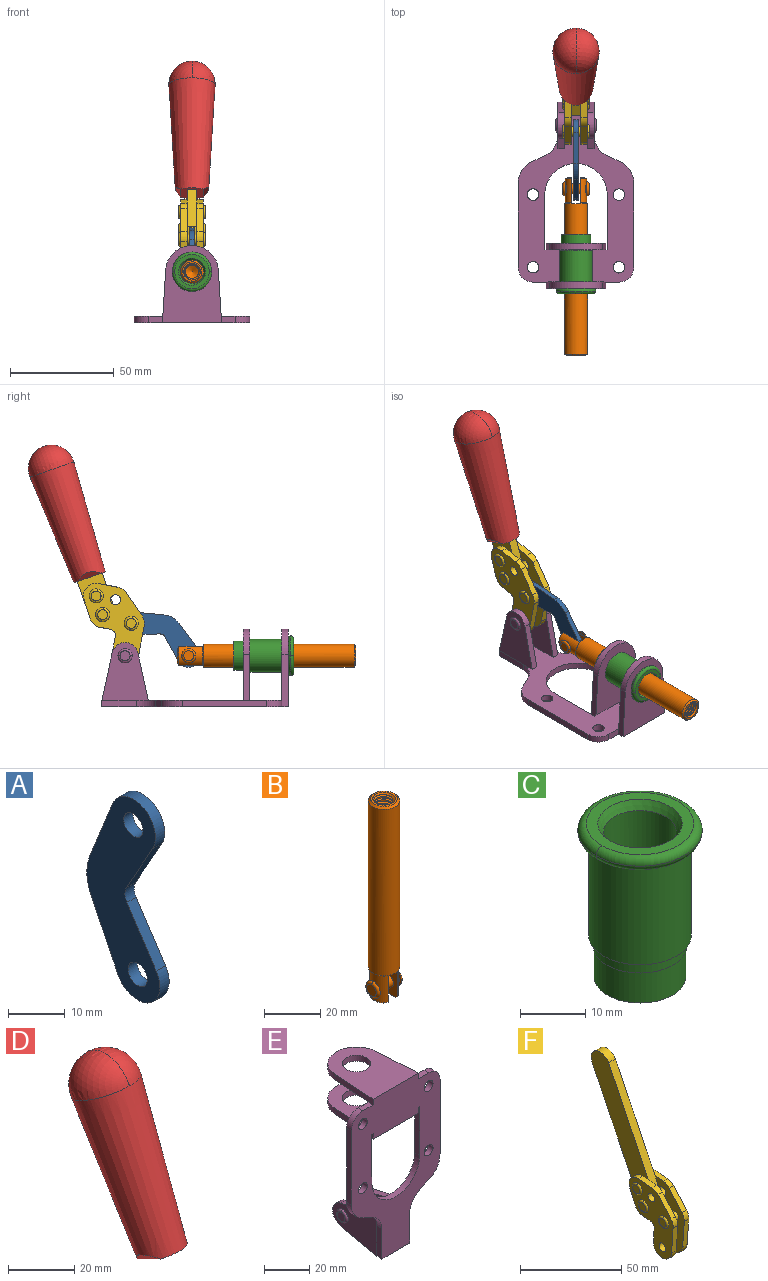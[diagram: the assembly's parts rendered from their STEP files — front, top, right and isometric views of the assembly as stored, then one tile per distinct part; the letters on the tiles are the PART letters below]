
ASSEMBLY  parts=6 mates=6
PART A: 12 faces, bbox 2.3x18.2x42.8 mm
  f0: cylinder r=2.4mm len=4.8mm, axis (1,0,0), area 34.9mm2, adj f4,f11
  f1: cylinder r=10.41mm len=8.47mm, axis (1,0,0), area 20.2mm2, adj f4,f9,f10,f11
  f2: cylinder r=3.05mm len=3.16mm, axis (1,0,0), area 7.7mm2, adj f4,f6,f7,f11
  f3: cylinder r=2.4mm len=4.8mm, axis (1,0,0), area 34.9mm2, adj f4,f11
  f4: plane 42.81x18.23mm, normal (-1,0,0), area 414.1mm2, adj f0,f1,f2,f3,f5,f6,f7,f8
  f5: cylinder r=5.54mm len=10.67mm, axis (1,0,0), area 41.8mm2, adj f4,f6,f10,f11
  f6: plane 11.66x6.53mm, normal (0,-0.87,-0.49), area 30.9mm2, adj f2,f4,f5,f11
  f7: plane 11.17x7.33mm, normal (0,-0.84,0.55), area 30.9mm2, adj f2,f4,f8,f11
  f8: cylinder r=5.54mm len=10.51mm, axis (1,0,0), area 41.8mm2, adj f4,f7,f9,f11
  f9: plane 13.67x6.67mm, normal (0,0.9,-0.44), area 35.1mm2, adj f1,f4,f8,f11
  f10: plane 14.1x5.7mm, normal (0,0.93,0.37), area 35.1mm2, adj f1,f4,f5,f11
  f11: plane 42.81x18.23mm, normal (1,0,0), area 414.1mm2, adj f0,f1,f2,f3,f5,f6,f7,f8
PART B: 48 faces, bbox 12.6x11.1x86.1 mm
  f0: torus R=2.41mm, axis (-1,0,0), area 15mm2, adj f30,f32,f34
  f1: torus R=2.41mm, axis (-1,0,0), area 15mm2, adj f29,f31,f33
  f2: cylinder r=5.54mm len=72.39mm, axis (0,0,1), area 2518.5mm2, adj f3,f4,f42,f43
  f3: cone r=5.54mm half-angle=45deg, axis (0,0,1), area 7.6mm2, adj f2,f5,f41
  f4: cone r=5.54mm half-angle=45deg, axis (0,0,-1), area 34.9mm2, adj f2,f39
  f5: cylinder r=5.08mm len=11.48mm, axis (0,0,1), area 108.3mm2, adj f3,f7,f8,f41
  f6: cylinder r=2.41mm len=4.83mm, axis (-1,0,0), area 71.2mm2, adj f40,f41
  f7: cylinder r=2.41mm len=4.83mm, axis (-1,0,0), area 7.6mm2, adj f5,f34
  f8: cone r=5.08mm half-angle=45deg, axis (0,0,1), area 10.6mm2, adj f5,f37,f41
  f9: cone r=3.98mm half-angle=45deg, axis (0,0,1), area 17.6mm2, adj f27,f39,f45,f46,f47
  f10: cylinder r=2.41mm len=4.83mm, axis (-1,0,0), area 7.6mm2, adj f33,f38
  f11: cylinder r=3.2mm len=6.4mm, axis (0,0,1), area 78.4mm2, adj f12,f28,f44,f45,f47
  f12: cylinder r=3.2mm len=6.4mm, axis (0,0,1), area 10.5mm2, adj f11,f13,f45,f47
  f13: cylinder r=3.2mm len=6.4mm, axis (0,0,1), area 10.5mm2, adj f12,f14,f45,f47
  f14: cylinder r=3.2mm len=6.4mm, axis (0,0,1), area 10.5mm2, adj f13,f15,f45,f47
  f15: cylinder r=3.2mm len=6.4mm, axis (0,0,1), area 10.5mm2, adj f14,f16,f45,f47
  f16: cylinder r=3.2mm len=6.4mm, axis (0,0,1), area 10.5mm2, adj f15,f17,f45,f47
  f17: cylinder r=3.2mm len=6.4mm, axis (0,0,1), area 10.5mm2, adj f16,f18,f45,f47
  f18: cylinder r=3.2mm len=6.4mm, axis (0,0,1), area 10.5mm2, adj f17,f19,f45,f47
  f19: cylinder r=3.2mm len=6.4mm, axis (0,0,1), area 10.5mm2, adj f18,f20,f45,f47
  f20: cylinder r=3.2mm len=6.4mm, axis (0,0,1), area 10.5mm2, adj f19,f21,f45,f47
  f21: cylinder r=3.2mm len=6.4mm, axis (0,0,1), area 10.5mm2, adj f20,f22,f45,f47
  f22: cylinder r=3.2mm len=6.4mm, axis (0,0,1), area 10.5mm2, adj f21,f23,f45,f47
  f23: cylinder r=3.2mm len=6.4mm, axis (0,0,1), area 10.5mm2, adj f22,f24,f45,f47
  f24: cylinder r=3.2mm len=6.4mm, axis (0,0,1), area 10.5mm2, adj f23,f25,f45,f47
  f25: cylinder r=3.2mm len=6.4mm, axis (0,0,1), area 10.5mm2, adj f24,f26,f45,f47
  f26: cylinder r=3.2mm len=6.4mm, axis (0,0,1), area 10.5mm2, adj f25,f27,f45,f47
  f27: cylinder r=3.2mm len=6.4mm, axis (0,0,1), area 7.4mm2, adj f9,f26,f45,f47
  f28: cone r=3.2mm half-angle=60deg, axis (0,0,1), area 37.2mm2, adj f11
  f29: plane 4.83x4.83mm, normal (-1,0,0), area 18.3mm2, adj f1,f31
  f30: plane 4.83x4.83mm, normal (1,0,0), area 18.3mm2, adj f0,f32
  f31: torus R=2.41mm, axis (-1,0,0), area 15mm2, adj f1,f29,f33
  f32: torus R=2.41mm, axis (-1,0,0), area 15mm2, adj f0,f30,f34
  f33: plane 6.83x6.83mm, normal (1,0,0), area 18.3mm2, adj f1,f10,f31
  f34: plane 6.83x6.83mm, normal (-1,0,0), area 18.3mm2, adj f0,f7,f32
  f35: cone r=5.08mm half-angle=45deg, axis (0,0,1), area 10.6mm2, adj f36,f38,f40
  f36: plane 7.25x1.97mm, normal (0,0,-1), area 10mm2, adj f35,f40
  f37: plane 7.25x1.97mm, normal (0,0,-1), area 10mm2, adj f8,f41
  f38: cylinder r=5.08mm len=11.48mm, axis (0,0,1), area 108.3mm2, adj f10,f35,f40,f42
  f39: plane 9.55x9.55mm, normal (0,0,1), area 22mm2, adj f4,f9
  f40: plane 12.76x10.09mm, normal (1,0,0), area 95.7mm2, adj f6,f35,f36,f38,f42,f43
  f41: plane 12.76x10.09mm, normal (-1,0,0), area 95.7mm2, adj f3,f5,f6,f8,f37,f43
  f42: cone r=5.54mm half-angle=45deg, axis (0,0,1), area 7.6mm2, adj f2,f38,f40
  f43: plane 11.07x4.7mm, normal (0,0,-1), area 50.4mm2, adj f2,f40,f41
  f44: plane 0.89x0.62mm, normal (-1,0,0), area 0.3mm2, adj f11,f45,f46,f47
  f45: bspline ~24.8x7.63mm, area 266.6mm2, adj f9,f11,f12,f13,f14,f15,f16,f17
  f46: bspline ~24.87x7.63mm, area 73.6mm2, adj f9,f44,f45,f47
  f47: bspline ~24.98x7.63mm, area 272.5mm2, adj f9,f11,f12,f13,f14,f15,f16,f17
PART C: 15 faces, bbox 20.6x20.6x28.7 mm
  f0: torus R=8.26mm, axis (0,0,1), area 56.8mm2, adj f1,f10,f12
  f1: torus R=8.26mm, axis (0,0,1), area 56.8mm2, adj f0,f6,f13
  f2: cylinder r=5.59mm len=25.91mm, axis (0,0,1), area 909.6mm2, adj f3,f4
  f3: cone r=6.86mm half-angle=45deg, axis (0,0,-1), area 70.2mm2, adj f2,f14
  f4: cone r=6.47mm half-angle=30deg, axis (0,0,1), area 66.7mm2, adj f2,f13
  f5: cylinder r=7.04mm len=14.07mm, axis (0,0,1), area 252.6mm2, adj f11,f14
  f6: torus R=8.26mm, axis (0,0,1), area 56.8mm2, adj f1,f12,f13
  f7: cylinder r=7.16mm len=14.33mm, axis (0,0,1), area 91.5mm2, adj f9,f11
  f8: cylinder r=7.86mm len=18.42mm, axis (0,0,1), area 909.6mm2, adj f9,f10
  f9: plane 15.72x15.72mm, normal (0,0,-1), area 33mm2, adj f7,f8
  f10: plane 16.51x16.51mm, normal (0,0,-1), area 19.9mm2, adj f0,f8,f12
  f11: plane 14.33x14.33mm, normal (0,0,-1), area 5.7mm2, adj f5,f7
  f12: torus R=8.26mm, axis (0,0,1), area 56.8mm2, adj f0,f6,f10
  f13: plane 16.51x16.51mm, normal (0,0,1), area 82.7mm2, adj f1,f4,f6
  f14: plane 14.07x14.07mm, normal (0,0,-1), area 7.8mm2, adj f3,f5
PART D: 11 faces, bbox 22.3x42.6x64.5 mm
  f0: sphere r=11.13mm, area 411.4mm2, adj f1,f8
  f1: cone r=11.11mm half-angle=3.3deg, axis (0,0.44,0.9), area 3251.8mm2, adj f0,f7,f8,f9,f10
  f2: cylinder r=6.16mm len=11.7mm, axis (1,0,0), area 89.5mm2, adj f3,f4,f5,f6
  f3: plane 60.23x36.75mm, normal (-1,0,0), area 763.6mm2, adj f2,f4,f6,f10
  f4: plane 51.37x25.05mm, normal (0,0.9,-0.44), area 264.2mm2, adj f2,f3,f5,f10
  f5: plane 60.23x36.75mm, normal (1,0,0), area 763.6mm2, adj f2,f4,f6,f10
  f6: plane 51.37x25.05mm, normal (0,-0.9,0.44), area 264.2mm2, adj f2,f3,f5,f10
  f7: plane 9.95x5.95mm, normal (0.71,-0.31,-0.64), area 25.8mm2, adj f1,f10
  f8: sphere r=11.13mm, area 411.4mm2, adj f0,f1
  f9: plane 9.95x5.95mm, normal (-0.71,-0.31,-0.64), area 25.8mm2, adj f1,f10
  f10: plane 14.27x11.38mm, normal (0,-0.44,-0.9), area 106.7mm2, adj f1,f3,f4,f5,f6,f7,f9
PART E: 55 faces, bbox 55.7x37.4x89.8 mm
  f0: torus R=2.41mm, axis (-1,0,0), area 15mm2, adj f11,f15,f25
  f1: torus R=2.41mm, axis (-1,0,0), area 15mm2, adj f10,f12,f22
  f2: cylinder r=2.78mm len=5.56mm, axis (0,-1,0), area 54.2mm2, adj f30,f54
  f3: cylinder r=14.99mm len=29.97mm, axis (0,-1,0), area 145.9mm2, adj f30,f49,f53,f54
  f4: cylinder r=2.78mm len=5.56mm, axis (0,-1,0), area 54.2mm2, adj f30,f54
  f5: cylinder r=2.78mm len=5.56mm, axis (0,-1,0), area 54.2mm2, adj f30,f54
  f6: cylinder r=2.78mm len=5.56mm, axis (0,-1,0), area 54.2mm2, adj f30,f54
  f7: cylinder r=6.35mm len=12.7mm, axis (0,0,1), area 123.6mm2, adj f27,f51
  f8: cylinder r=6.35mm len=12.7mm, axis (0,0,-1), area 124.7mm2, adj f21,f35
  f9: cylinder r=2.41mm len=11.18mm, axis (-1,0,0), area 169.4mm2, adj f16,f19
  f10: plane 4.83x4.83mm, normal (1,0,0), area 18.3mm2, adj f1,f12
  f11: plane 4.83x4.83mm, normal (-1,0,0), area 18.3mm2, adj f0,f15
  f12: torus R=2.41mm, axis (-1,0,0), area 15mm2, adj f1,f10,f22
  f13: cylinder r=6.35mm len=12.41mm, axis (1,0,0), area 53.4mm2, adj f18,f19,f22,f23
  f14: cylinder r=6.35mm len=12.41mm, axis (-1,0,0), area 53.4mm2, adj f16,f17,f24,f25
  f15: torus R=2.41mm, axis (-1,0,0), area 15mm2, adj f0,f11,f25
  f16: plane 27.86x22.35mm, normal (1,0,0), area 425.4mm2, adj f9,f14,f17,f24,f30
  f17: plane 22.86x4.97mm, normal (0,0.21,0.98), area 72.5mm2, adj f14,f16,f25,f30
  f18: plane 22.86x4.97mm, normal (0,0.21,0.98), area 72.5mm2, adj f13,f19,f22,f30
  f19: plane 27.86x22.35mm, normal (-1,0,0), area 425.4mm2, adj f9,f13,f18,f23,f30
  f20: cylinder r=12.7mm len=25.35mm, axis (0,0,-1), area 119.8mm2, adj f21,f34,f35,f36
  f21: plane 34.21x28.07mm, normal (0,0,-1), area 702.4mm2, adj f8,f20,f30,f34,f36
  f22: plane 27.96x22.45mm, normal (1,0,0), area 407.2mm2, adj f1,f12,f13,f18,f23,f30,f42,f43
  f23: plane 22.86x4.97mm, normal (0,0.21,-0.98), area 72.5mm2, adj f13,f19,f22,f44
  f24: plane 22.86x4.97mm, normal (0,0.21,-0.98), area 72.5mm2, adj f14,f16,f25,f44
  f25: plane 27.86x22.35mm, normal (-1,0,0), area 407.1mm2, adj f0,f14,f15,f17,f24,f30,f45,f46
  f26: plane 3.1x0.95mm, normal (0,0,-1), area 2.7mm2, adj f30,f49,f50,f54
  f27: plane 34.21x28.07mm, normal (0,0,1), area 702.4mm2, adj f7,f28,f30,f50,f52
  f28: cylinder r=12.7mm len=25.35mm, axis (0,0,1), area 118.8mm2, adj f27,f50,f51,f52
  f29: plane 3.1x0.95mm, normal (0,0,-1), area 2.7mm2, adj f30,f52,f53,f54
  f30: plane 86.54x55.63mm, normal (0,1,0), area 2362.9mm2, adj f2,f3,f4,f5,f6,f16,f17,f18
  f31: plane 40.56x3.1mm, normal (-1,0,0), area 125.7mm2, adj f30,f32,f48,f54
  f32: cylinder r=7.11mm len=7.11mm, axis (0,-1,0), area 34.6mm2, adj f30,f31,f33,f54
  f33: plane 6.67x3.1mm, normal (0,0,1), area 20.4mm2, adj f30,f32,f34,f54
  f34: plane 25.39x3.13mm, normal (-1,0.06,0), area 79.5mm2, adj f20,f21,f33,f35,f54
  f35: plane 37.31x28.45mm, normal (0,0,1), area 789.9mm2, adj f8,f20,f34,f36,f54
  f36: plane 25.39x3.13mm, normal (1,0.06,0), area 79.5mm2, adj f20,f21,f35,f37,f54
  f37: plane 6.67x3.1mm, normal (0,0,1), area 20.4mm2, adj f30,f36,f38,f54
  f38: cylinder r=7.11mm len=7.11mm, axis (0,-1,0), area 34.6mm2, adj f30,f37,f39,f54
  f39: plane 40.56x3.1mm, normal (1,0,0), area 125.7mm2, adj f30,f38,f40,f54
  f40: cylinder r=11.18mm len=10.16mm, axis (0,-1,0), area 39.5mm2, adj f30,f39,f41,f54
  f41: plane 6.09x3.1mm, normal (0.42,0,-0.91), area 20.8mm2, adj f30,f40,f42,f54
  f42: cylinder r=11.18mm len=9.41mm, axis (0,-1,0), area 37.2mm2, adj f22,f30,f41,f43,f54
  f43: plane 16.5x3.1mm, normal (1,0,0), area 51.1mm2, adj f22,f42,f44,f54
  f44: plane 17.37x3.1mm, normal (0,0,-1), area 53.8mm2, adj f23,f24,f30,f43,f45,f54
  f45: plane 16.5x3.1mm, normal (-1,0,0), area 51.1mm2, adj f25,f44,f46,f54
  f46: cylinder r=11.18mm len=9.41mm, axis (0,-1,0), area 37.2mm2, adj f25,f30,f45,f47,f54
  f47: plane 6.09x3.1mm, normal (-0.42,0,-0.91), area 20.8mm2, adj f30,f46,f48,f54
  f48: cylinder r=11.18mm len=10.16mm, axis (0,-1,0), area 39.5mm2, adj f30,f31,f47,f54
  f49: plane 26.54x3.1mm, normal (-1,0,0), area 82.3mm2, adj f3,f26,f30,f54
  f50: plane 25.39x3.1mm, normal (1,0.06,0), area 78.8mm2, adj f26,f27,f28,f51,f54
  f51: plane 37.31x28.45mm, normal (0,0,-1), area 789.9mm2, adj f7,f28,f50,f52,f54
  f52: plane 25.39x3.1mm, normal (-1,0.06,0), area 78.8mm2, adj f27,f28,f29,f51,f54
  f53: plane 26.54x3.1mm, normal (1,0,0), area 82.3mm2, adj f3,f29,f30,f54
  f54: plane 89.66x55.63mm, normal (0,-1,0), area 2678.5mm2, adj f2,f3,f4,f5,f6,f26,f29,f31
PART F: 59 faces, bbox 12.9x60.2x99.6 mm
  f0: torus R=2.39mm, axis (-1,0,0), area 14.9mm2, adj f20,f43,f51
  f1: torus R=2.39mm, axis (-1,0,0), area 14.9mm2, adj f19,f42,f51
  f2: torus R=2.39mm, axis (-1,0,0), area 14.9mm2, adj f18,f35,f51
  f3: torus R=2.39mm, axis (-1,0,0), area 14.9mm2, adj f14,f17,f23
  f4: torus R=2.39mm, axis (-1,0,0), area 14.9mm2, adj f13,f16,f23
  f5: torus R=2.39mm, axis (-1,0,0), area 14.9mm2, adj f12,f15,f23
  f6: cylinder r=2.39mm len=4.78mm, axis (1,0,0), area 46.5mm2, adj f48,f50,f51
  f7: cylinder r=2.39mm len=4.78mm, axis (1,0,0), area 46.5mm2, adj f50,f51
  f8: cylinder r=6.35mm len=12.68mm, axis (1,0,0), area 61.8mm2, adj f38,f39,f50,f51
  f9: cylinder r=2.39mm len=4.78mm, axis (-1,0,0), area 70.5mm2, adj f46,f50
  f10: cylinder r=2.39mm len=4.78mm, axis (-1,0,0), area 46.5mm2, adj f23,f45,f46
  f11: cylinder r=2.39mm len=4.78mm, axis (-1,0,0), area 46.5mm2, adj f23,f46
  f12: plane 4.78x4.78mm, normal (1,0,0), area 17.9mm2, adj f5,f15
  f13: plane 4.78x4.78mm, normal (1,0,0), area 17.9mm2, adj f4,f16
  f14: plane 4.78x4.78mm, normal (1,0,0), area 17.9mm2, adj f3,f17
  f15: torus R=2.39mm, axis (-1,0,0), area 14.9mm2, adj f5,f12,f23
  f16: torus R=2.39mm, axis (-1,0,0), area 14.9mm2, adj f4,f13,f23
  f17: torus R=2.39mm, axis (-1,0,0), area 14.9mm2, adj f3,f14,f23
  f18: plane 4.78x4.78mm, normal (-1,0,0), area 17.9mm2, adj f2,f35
  f19: plane 4.78x4.78mm, normal (-1,0,0), area 17.9mm2, adj f1,f42
  f20: plane 4.78x4.78mm, normal (-1,0,0), area 17.9mm2, adj f0,f43
  f21: plane 2.26x0.2mm, normal (1,0,0), area 0.2mm2, adj f31,f44
  f22: plane 2.26x0.2mm, normal (-1,0,0), area 0.2mm2, adj f41,f44
  f23: plane 39.37x30.77mm, normal (1,0,0), area 565.5mm2, adj f3,f4,f5,f10,f11,f15,f16,f17
  f24: cylinder r=6.1mm len=4.15mm, axis (-1,0,0), area 14.7mm2, adj f23,f25,f32,f46
  f25: plane 10.25x9.01mm, normal (0,-0.75,0.66), area 42.3mm2, adj f23,f24,f26,f46
  f26: cylinder r=6.35mm len=4.64mm, axis (-1,0,0), area 15.6mm2, adj f23,f25,f27,f46
  f27: plane 15.84x3.1mm, normal (0,-1,-0.07), area 49.2mm2, adj f23,f26,f28,f46
  f28: cylinder r=6.35mm len=12.68mm, axis (-1,0,0), area 61.8mm2, adj f23,f27,f29,f46
  f29: plane 8.11x3.1mm, normal (0,1,0.07), area 25.2mm2, adj f23,f28,f30,f46
  f30: cylinder r=3.05mm len=3.25mm, axis (-1,0,0), area 14.8mm2, adj f23,f29,f31,f46
  f31: plane 5.99x3.1mm, normal (0,0.07,-1), area 18.6mm2, adj f21,f23,f30,f44,f46
  f32: plane 9.5x3.1mm, normal (0,-0.07,1), area 29.5mm2, adj f23,f24,f33,f46,f47
  f33: cylinder r=6.1mm len=8.63mm, axis (-1,0,0), area 39.1mm2, adj f23,f32,f34,f47
  f34: plane 8.65x3.96mm, normal (0,0.91,-0.42), area 29.5mm2, adj f23,f33,f44,f47
  f35: torus R=2.39mm, axis (-1,0,0), area 14.9mm2, adj f2,f18,f51
  f36: plane 10.25x9.01mm, normal (0,-0.75,0.66), area 42.3mm2, adj f37,f49,f50,f51
  f37: cylinder r=6.35mm len=4.64mm, axis (1,0,0), area 15.6mm2, adj f36,f38,f50,f51
  f38: plane 15.84x3.1mm, normal (0,-1,-0.07), area 49.2mm2, adj f8,f37,f50,f51
  f39: plane 8.11x3.1mm, normal (0,1,0.07), area 25.2mm2, adj f8,f40,f50,f51
  f40: cylinder r=3.05mm len=3.25mm, axis (1,0,0), area 14.8mm2, adj f39,f41,f50,f51
  f41: plane 5.99x3.1mm, normal (0,0.07,-1), area 18.6mm2, adj f22,f40,f44,f50,f51
  f42: torus R=2.39mm, axis (-1,0,0), area 14.9mm2, adj f1,f19,f51
  f43: torus R=2.39mm, axis (-1,0,0), area 14.9mm2, adj f0,f20,f51
  f44: cylinder r=6.35mm len=12.12mm, axis (-1,0,0), area 128.9mm2, adj f21,f22,f23,f31,f34,f41,f46,f47
  f45: plane 2.65x1.35mm, normal (1,0,0), area 1mm2, adj f10,f55
  f46: plane 39.08x20.42mm, normal (-1,0,0), area 412.5mm2, adj f9,f10,f11,f24,f25,f26,f27,f28
  f47: plane 77.62x39.82mm, normal (1,0,0), area 850mm2, adj f32,f33,f34,f44,f53,f54,f55
  f48: plane 2.65x1.35mm, normal (-1,0,0), area 1mm2, adj f6,f55
  f49: cylinder r=6.1mm len=4.15mm, axis (1,0,0), area 14.7mm2, adj f36,f50,f51,f56
  f50: plane 39.08x20.42mm, normal (1,0,0), area 412.5mm2, adj f6,f7,f8,f9,f36,f37,f38,f39
  f51: plane 39.37x30.77mm, normal (-1,0,0), area 565.5mm2, adj f0,f1,f2,f6,f7,f8,f35,f36
  f52: plane 8.65x3.96mm, normal (0,0.91,-0.42), area 29.5mm2, adj f44,f51,f57,f58
  f53: plane 68.49x33.4mm, normal (0,0.9,-0.44), area 358.1mm2, adj f44,f47,f54,f58
  f54: cylinder r=6.35mm len=12.06mm, axis (1,0,0), area 93.7mm2, adj f47,f53,f55,f58
  f55: plane 68.49x33.4mm, normal (0,-0.9,0.44), area 358.1mm2, adj f44,f45,f46,f47,f48,f50,f54,f58
  f56: plane 9.5x3.1mm, normal (0,-0.07,1), area 29.5mm2, adj f49,f50,f51,f57,f58
  f57: cylinder r=6.1mm len=8.63mm, axis (1,0,0), area 39.1mm2, adj f51,f52,f56,f58
  f58: plane 77.62x39.82mm, normal (-1,0,0), area 850mm2, adj f44,f52,f53,f54,f55,f56,f57
PLACE A rot(axis=(1,0,0),121.4deg) t=(0,36.95,11.68)mm
PLACE B rot(axis=(1,0,0),90deg) t=(0,26.38,0)mm
PLACE C rot(axis=(1,0,0),90deg) t=(0,9.43,0)mm
PLACE D rot(axis=(1,0,0),6.7deg) t=(0,13.32,53.6)mm
PLACE E rot(axis=(1,0,0),90deg) t=(0,9.43,0)mm fixed
PLACE F rot(axis=(1,0,0),6.7deg) t=(0,13.32,53.6)mm
MATE revolute F.f7 <-> E.f0  axis (1,0,0) through (0,41.52,24.61)mm
MATE revolute A.f5 <-> B.f6  axis (1,0,0) through (0,10.91,24.61)mm
MATE fastened D.f2 <-> F.f54  axis (1,0,0) through (0,77.44,116.32)mm
MATE fastened C.f0 <-> E.f7  axis (0,1,0) through (0,-36.96,24.61)mm
MATE revolute A.f3 <-> F.f4  axis (1,0,0) through (0,38.57,40.21)mm
MATE slider B.f2 <-> C.f2  axis (0,-1,0) through (0,-32.4,24.61)mm
